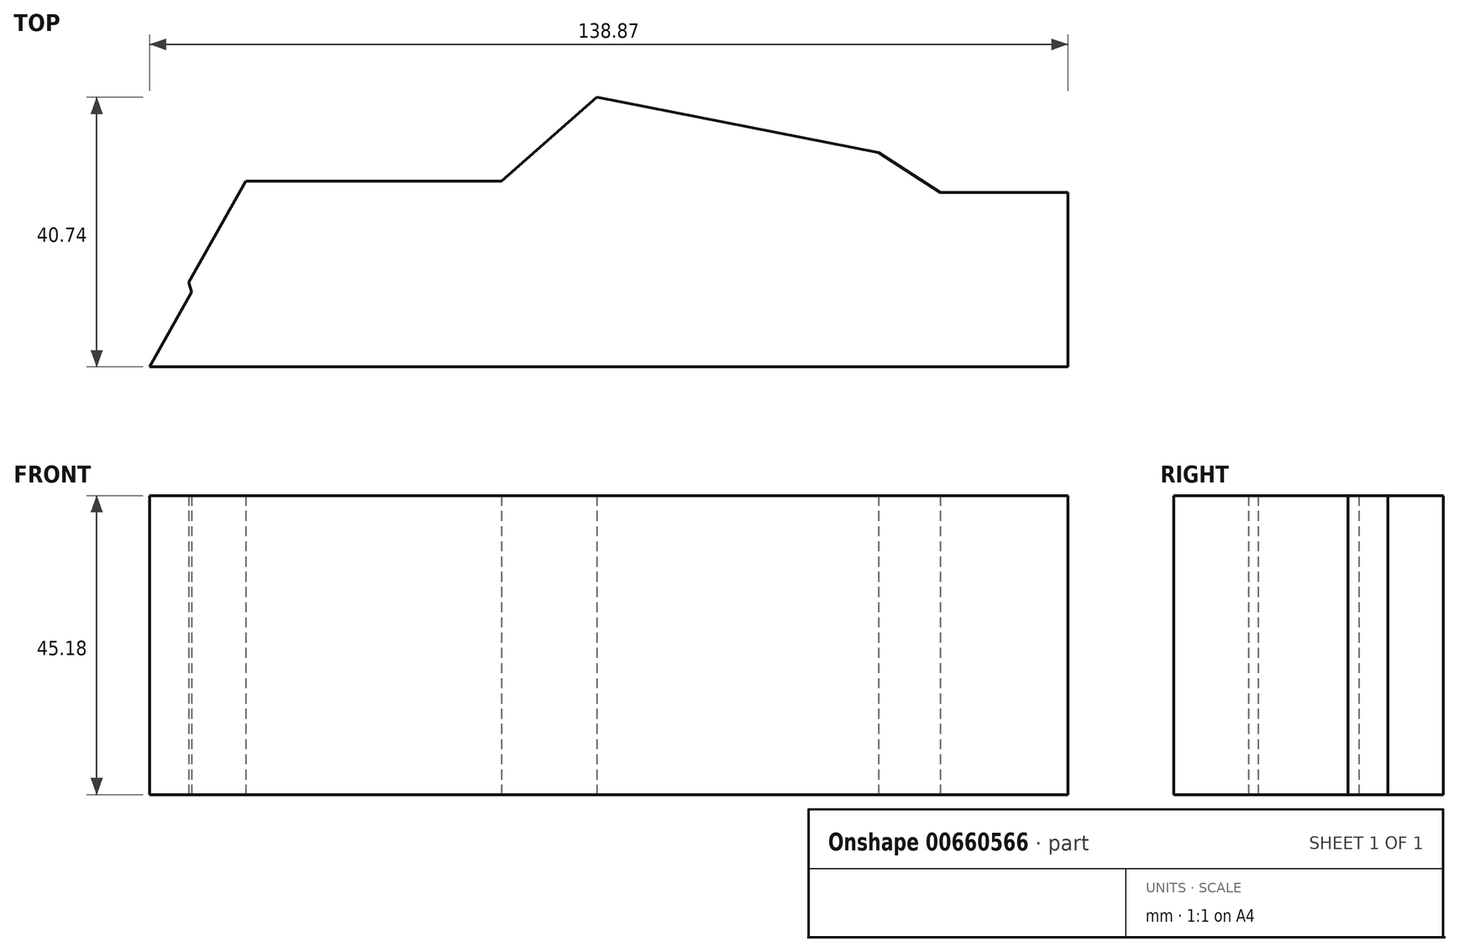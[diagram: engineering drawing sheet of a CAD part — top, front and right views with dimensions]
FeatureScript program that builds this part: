
annotation { "Feature Type Name" : "Feature", "Feature Type Description" : "" }
export const myFeature = defineFeature(function(context is Context, id is Id, definition is map)
    precondition{}
    {
        {
            var Q0;
            Q0=qCreatedBy(makeId("Top.planeOp"),FACE);
            var sketch = newSketch(context, id + "F0", { "sketchPlane" : qUnion([Q0])});
            skLineSegment(sketch, "E0", {"start": v(-61.69, 0) * mm, "end": v(-53.04, 15.3) * mm});
            skLineSegment(sketch, "E1", {"start": v(-53.04, 15.3) * mm, "end": v(-14.4, 15.3) * mm});
            skLineSegment(sketch, "E2", {"start": v(-14.4, 15.3) * mm, "end": v(0, 28) * mm});
            skLineSegment(sketch, "E3", {"start": v(0, 28) * mm, "end": v(42.6, 19.62) * mm});
            skLineSegment(sketch, "E4", {"start": v(42.6, 19.62) * mm, "end": v(52, 13.65) * mm});
            skLineSegment(sketch, "E5", {"start": v(52, 13.65) * mm, "end": v(71.27, 13.65) * mm});
            skLineSegment(sketch, "E6", {"start": v(71.27, 13.65) * mm, "end": v(71.27, -12.74) * mm});
            skLineSegment(sketch, "E7", {"start": v(71.27, -12.74) * mm, "end": v(-49.15, -12.74) * mm});
            skLineSegment(sketch, "E8", {"start": v(-49.15, -12.74) * mm, "end": v(-67.6, -12.74) * mm});
            skLineSegment(sketch, "E9", {"start": v(-67.6, -12.74) * mm, "end": v(-61.28, -1.44) * mm});
            skLineSegment(sketch, "E10", {"start": v(-61.28, -1.44) * mm, "end": v(-61.69, 0) * mm});
            skSolve(sketch);
        }
        {
            var Q0;
            Q0 = qSketchRegion(id + "F0", true);
            extrude(context, id + "F1", {"entities" : qUnion([Q0]), "endBound" : BoundingType.SYMMETRIC, "depth" : 45.18 * mm, "offsetDistance" : 25.4 * mm});
        }
    });
